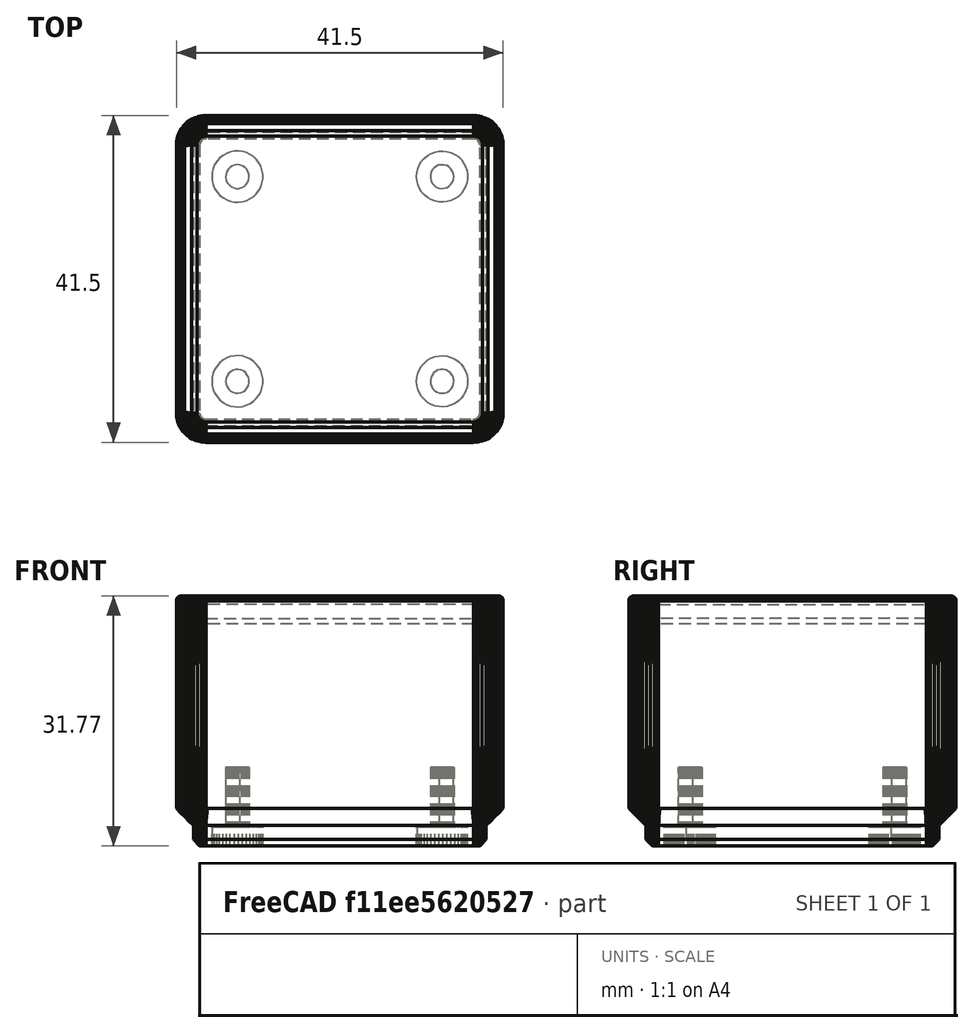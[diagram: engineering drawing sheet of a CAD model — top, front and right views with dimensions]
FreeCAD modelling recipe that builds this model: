
FCSTD DOCUMENT  (FreeCAD 0.20R29410 (Git))
Label: 1x1_plain
License: All rights reserved
LicenseURL: http://en.wikipedia.org/wiki/All_rights_reserved
objects: Part::Feature×2, Mesh::Feature×1, Part::Refine×1, PartDesign::FeatureBase×1, PartDesign::Body×1
note: 5 computed .brp shape members not serialized (recipe doc carries the construction recipe); baked Part::Feature solids carry a one-line shape summary decoded from their .brp

FEATURE [Mesh::Feature] _x1_Block_1_25in  label="1x1 Block 1.25in"
FEATURE [Part::Feature] _x1_Block_1_25in001
  shape: bbox 41.5 x 41.5 x 31.77 mm, 5878 faces, 0 solids (baked)
FEATURE [Part::Refine] _x1_Block_1_25in001001
  Source = -> _x1_Block_1_25in001
FEATURE [Part::Feature] _x1_Block_1_25in001001_solid  label="_x1_Block_1_25in001001 (Solid)"
  shape: bbox 41.5 x 41.5 x 31.77 mm, 4300 faces (baked)
FEATURE [PartDesign::FeatureBase] BaseFeature
  BaseFeature = -> _x1_Block_1_25in001001_solid
FEATURE [PartDesign::Body] Body
  BaseFeature = -> _x1_Block_1_25in001001_solid
  Group = -> [BaseFeature]
  Origin = -> Origin
  Tip = -> BaseFeature
